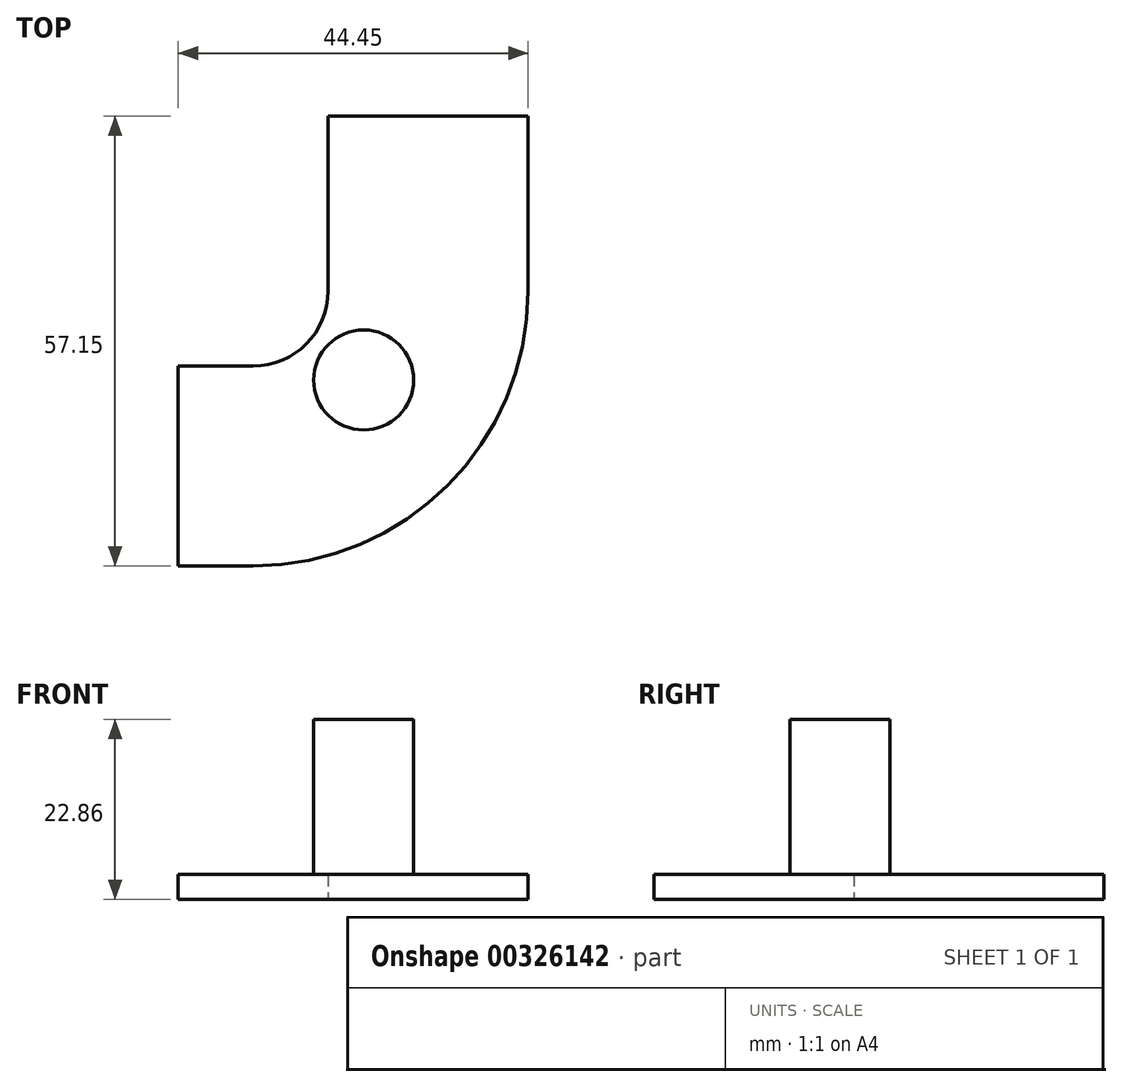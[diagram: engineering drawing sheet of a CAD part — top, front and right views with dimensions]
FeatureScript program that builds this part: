
annotation { "Feature Type Name" : "Feature", "Feature Type Description" : "" }
export const myFeature = defineFeature(function(context is Context, id is Id, definition is map)
    precondition{}
    {
        {
            var Q0;
            Q0=qCreatedBy(makeId("Top.planeOp"),FACE);
            var sketch = newSketch(context, id + "F0", { "sketchPlane" : qUnion([Q0])});
            skLineSegment(sketch, "E0", {"start": v(-25.4, 57.15) * mm, "end": v(-25.4, 34.92) * mm});
            skLineSegment(sketch, "E1", {"start": v(9.53, 0) * mm, "end": v(19.05, 0) * mm});
            skLineSegment(sketch, "E2", {"start": v(19.05, 0) * mm, "end": v(19.05, 25.4) * mm});
            skLineSegment(sketch, "E3", {"start": v(19.05, 25.4) * mm, "end": v(9.53, 25.4) * mm});
            skLineSegment(sketch, "E4", {"start": v(-25.4, 57.15) * mm, "end": v(0, 57.15) * mm});
            skLineSegment(sketch, "E5", {"start": v(0, 57.15) * mm, "end": v(0, 34.93) * mm});
            skPoint(sketch, "E6.visualSharp", {"position": v(0, 25.4) * mm});
            skArc(sketch, "E6.filletArc", {"start": v(0, 34.93) * mm, "mid": v(2.79, 28.19) * mm, "end": v(9.53, 25.4) * mm});
            skPoint(sketch, "E7.visualSharp", {"position": v(-25.4, 0) * mm});
            skArc(sketch, "E7.filletArc", {"start": v(-25.4, 34.92) * mm, "mid": v(-15.17, 10.23) * mm, "end": v(9.53, 0) * mm});
            skCircle(sketch, "E8", {"center": v(-4.5, 23.62) * mm, "radius": 6.35 * mm});
            skSolve(sketch);
        }
        {
            var Q0;
            Q0=makeQuery(id+"F0.imprint","IMPRINT",FACE,{"disambiguationData":[TD([[makeQuery(id+"F0.imprint","IMPRINT",EDGE,{"derivedFrom":sQuery(id+"F0.wireOp",EDGE,"E8")}),1.0]])]});
            extrude(context, id + "F1", {"entities" : qUnion([Q0]), "depth" : -22.86 * mm});
        }
        {
            var Q0;
            Q0=qSketchRegion(id+"F0",true);
            extrude(context, id + "F2", {"entities" : qUnion([Q0]), "operationType" : NewBodyOperationType.ADD, "depth" : -3.17 * mm});
        }
        {
            var Q0;
            Q0=makeQuery(id+"F1.opExtrude","SWEPT_BODY",BODY,{"disambiguationData":[OSD([sQuery(id+"F0.wireOp",EDGE,"E8")])]});
            var Q1;
            Q1=makeQuery(id+"F2.opExtrude","CAP_EDGE",EDGE,{"disambiguationData":[OSD([sQuery(id+"F0.wireOp",EDGE,"E5")])],"isStart":false});
            transform(context, id + "F3", {"entities" : qUnion([Q0]), "transformType" : TransformType.ROTATION, "transformAxis" : qUnion([Q1]), "angle" : 180 * degree, "makeCopy" : false});
        }
    });
